# Revit family: Trane_TVR_Indoor_Ceiling & Floor_4TVX0038(48)EF000AA(2nd DC)
name_source: partatom
category: Equipamento mecânico
units: mm (PartAtom-declared; Revit-internal decimal feet)

## family parameters
Com base no plano de trabalho = Não
Compartilhado = Não
Corte com vazios quando carregada = Não
Cota do conector redondo = Utilizar diâmetro
Número OmniClass = 23.75.00.00
Ponto de cálculo do ambiente = Não
Sempre na vertical = Sim
Tipo de parte = Normal
Título OmniClass = Climate Control (HVAC)

## types (2) — shared parameters
Condensation = air
Cooling Power Input = 180 W
Depth = 680  [stored 2.23097 ft]
Descrição = High efficiency air cooled
Fabricante = Trane
Gas = R410a
Gas pipe = 15.9  [stored 0.0521654 ft]
Heating Power Input = 180 W
Height = 244  [stored 0.800525 ft]
Installation = Indoor installation
Liquid pipe = 9.53
MCA (Minimum Circuit Amps) = 1 A
MFA (Maximum Fuse Amps) = 15 A
Machine material = Galvanized Steel
Net Weight = 48.00 kg
Panel color = S1004
Power supply = 220-240V ~50/60Hz
URL = https://www.trane.com
Width = 1670

## per-type parameters (varying)
| type | Air  Flow | Cooling Capacity | Heating Capacity | Series |
| 4TVX0038EF000AA | 1890/1830/1765/1700/1660/1620/1580 m3/h | 11 kW | 13 kW | TVR ULTRA |
| 4TVX0048EF000AA | 1980/1940/1900/1860/1810/1770/1730 m3/h | 14 kW | 15 kW | TVR LX |

note: column(s) folded — value = type name in every type: Modelo

note: [stored X ft] marks values corroborated as IEEE doubles in the binary element streams (Revit-internal decimal feet)
